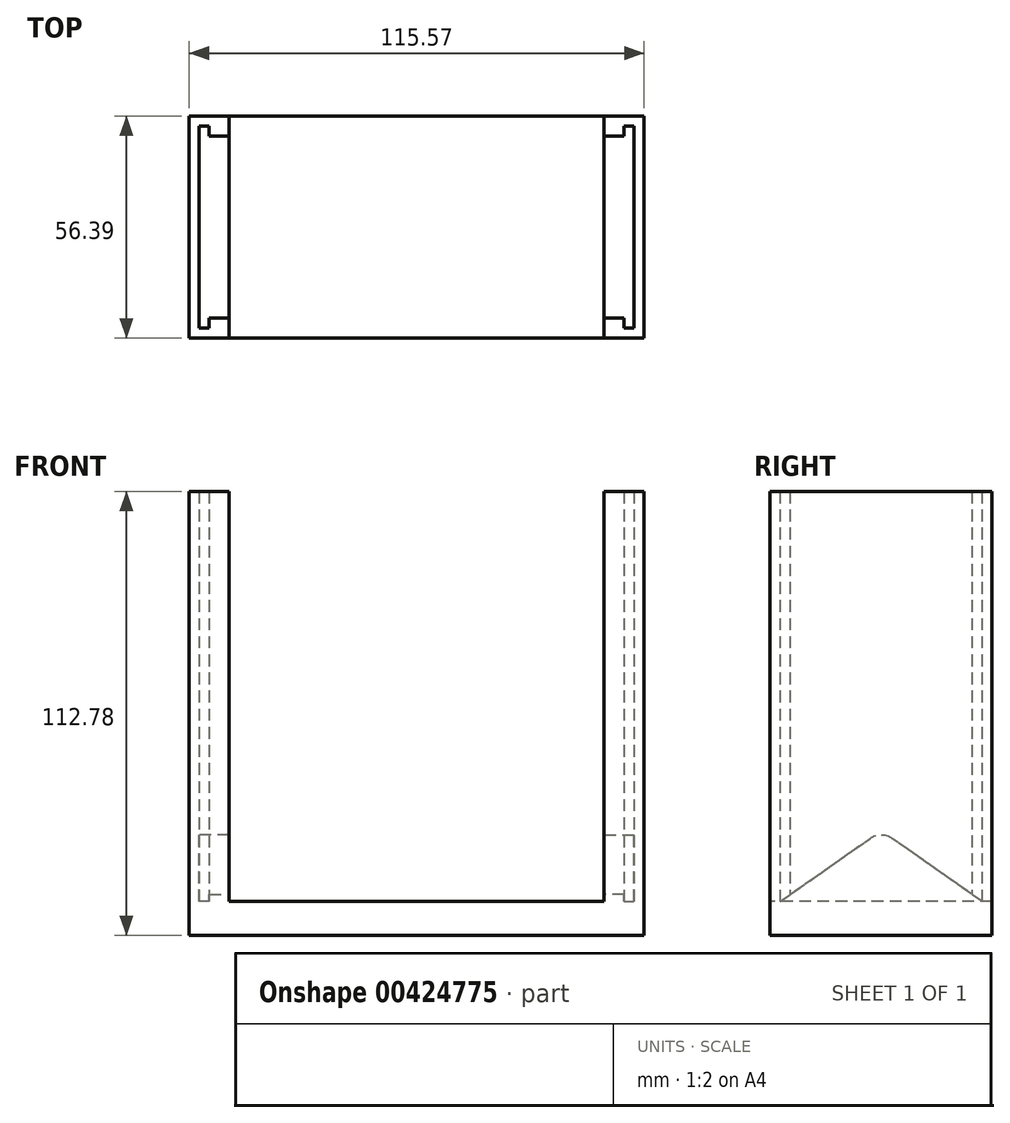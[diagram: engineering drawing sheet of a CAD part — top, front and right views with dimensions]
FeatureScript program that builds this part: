
annotation { "Feature Type Name" : "Feature", "Feature Type Description" : "" }
export const myFeature = defineFeature(function(context is Context, id is Id, definition is map)
    precondition{}
    {
        {
            var Q0;
            Q0=qCreatedBy(makeId("Top.planeOp"),FACE);
            var sketch = newSketch(context, id + "F0", { "sketchPlane" : qUnion([Q0])});
            skLineSegment(sketch, "E0.bottom", {"start": v(-115.57, 0) * mm, "end": v(0, 0) * mm});
            skLineSegment(sketch, "E0.top", {"start": v(-115.57, -56.39) * mm, "end": v(0, -56.39) * mm});
            skLineSegment(sketch, "E0.left", {"start": v(-115.57, 0) * mm, "end": v(-115.57, -56.39) * mm});
            skLineSegment(sketch, "E0.right", {"start": v(0, 0) * mm, "end": v(0, -56.39) * mm});
            skSolve(sketch);
        }
        {
            var Q0;
            Q0=qSketchRegion(id+"F0",true);
            extrude(context, id + "F1", {"entities" : qUnion([Q0]), "depth" : 8.64 * mm});
        }
        {
            var Q0;
            Q0=makeQuery(id+"F1.opExtrude","CAP_FACE",FACE,{"disambiguationData":[OSD([sQuery(id+"F0.wireOp",EDGE,"E0.bottom"),sQuery(id+"F0.wireOp",EDGE,"E0.top"),sQuery(id+"F0.wireOp",EDGE,"E0.left"),sQuery(id+"F0.wireOp",EDGE,"E0.right")])],"isStart":false});
            var sketch = newSketch(context, id + "F2", { "sketchPlane" : qUnion([Q0])});
            skLineSegment(sketch, "E1", {"start": v(0, -28.2) * mm, "end": v(0, -56.39) * mm});
            skLineSegment(sketch, "E2", {"start": v(0, -56.39) * mm, "end": v(-10.16, -56.39) * mm});
            skLineSegment(sketch, "E3", {"start": v(-10.16, -56.39) * mm, "end": v(-10.16, -51.3) * mm});
            skLineSegment(sketch, "E4", {"start": v(-10.16, -51.3) * mm, "end": v(-5.08, -51.3) * mm});
            skLineSegment(sketch, "E5", {"start": v(-5.08, -51.3) * mm, "end": v(-5.08, -53.85) * mm});
            skLineSegment(sketch, "E6", {"start": v(-5.08, -53.85) * mm, "end": v(-2.54, -53.85) * mm});
            skLineSegment(sketch, "E7", {"start": v(-2.54, -53.85) * mm, "end": v(-2.54, -28.2) * mm});
            skLineSegment(sketch, "E8", {"start": v(0, -28.2) * mm, "end": v(-115.57, -28.2) * mm, "construction": true});
            skLineSegment(sketch, "E9", {"start": v(-57.79, 0) * mm, "end": v(-57.79, -56.39) * mm, "construction": true});
            skLineSegment(sketch, "E10.MirrorCS", {"start": v(-2.54, -2.54) * mm, "end": v(-2.54, -28.2) * mm});
            skLineSegment(sketch, "E11.MirrorCS", {"start": v(0, -28.2) * mm, "end": v(0, 0) * mm});
            skLineSegment(sketch, "E12.MirrorCS", {"start": v(-5.08, -2.54) * mm, "end": v(-2.54, -2.54) * mm});
            skLineSegment(sketch, "E13.MirrorCS", {"start": v(0, 0) * mm, "end": v(-10.16, 0) * mm});
            skLineSegment(sketch, "E14.MirrorCS", {"start": v(-10.16, 0) * mm, "end": v(-10.16, -5.08) * mm});
            skLineSegment(sketch, "E15.MirrorCS", {"start": v(-10.16, -5.08) * mm, "end": v(-5.08, -5.08) * mm});
            skLineSegment(sketch, "E16.MirrorCS", {"start": v(-5.08, -5.08) * mm, "end": v(-5.08, -2.54) * mm});
            skLineSegment(sketch, "E17.MirrorCS", {"start": v(-105.4, 0) * mm, "end": v(-105.4, -5.08) * mm});
            skLineSegment(sketch, "E18.MirrorCS", {"start": v(-105.4, -5.08) * mm, "end": v(-110.5, -5.08) * mm});
            skLineSegment(sketch, "E19.MirrorCS", {"start": v(-110.49, -5.08) * mm, "end": v(-110.49, -2.54) * mm});
            skLineSegment(sketch, "E20.MirrorCS", {"start": v(-110.5, -2.54) * mm, "end": v(-113.03, -2.54) * mm});
            skLineSegment(sketch, "E21.MirrorCS", {"start": v(-115.57, 0) * mm, "end": v(-105.41, 0) * mm});
            skLineSegment(sketch, "E22.MirrorCS", {"start": v(-113.03, -2.54) * mm, "end": v(-113.03, -28.2) * mm});
            skLineSegment(sketch, "E23.MirrorCS", {"start": v(-115.57, -28.2) * mm, "end": v(-115.57, 0) * mm});
            skLineSegment(sketch, "E24.MirrorCS", {"start": v(-115.57, -28.2) * mm, "end": v(-115.57, -56.39) * mm});
            skLineSegment(sketch, "E25.MirrorCS", {"start": v(-113.03, -53.85) * mm, "end": v(-113.03, -28.2) * mm});
            skLineSegment(sketch, "E26.MirrorCS", {"start": v(-110.5, -53.85) * mm, "end": v(-113.03, -53.85) * mm});
            skLineSegment(sketch, "E27.MirrorCS", {"start": v(-115.57, -56.39) * mm, "end": v(-105.41, -56.39) * mm});
            skLineSegment(sketch, "E28.MirrorCS", {"start": v(-105.4, -56.39) * mm, "end": v(-105.4, -51.3) * mm});
            skLineSegment(sketch, "E29.MirrorCS", {"start": v(-105.4, -51.3) * mm, "end": v(-110.5, -51.3) * mm});
            skLineSegment(sketch, "E30.MirrorCS", {"start": v(-110.49, -51.3) * mm, "end": v(-110.49, -53.85) * mm});
            skSolve(sketch);
        }
        {
            var Q0;
            Q0=qSketchRegion(id+"F2",true);
            extrude(context, id + "F3", {"entities" : qUnion([Q0]), "operationType" : NewBodyOperationType.ADD, "depth" : 104.14 * mm});
        }
        {
            var Q0;
            Q0=makeQuery(id+"F3.opExtrude","SWEPT_FACE",FACE,{"disambiguationData":[OSD([sQuery(id+"F2.wireOp",EDGE,"E22.MirrorCS"),sQuery(id+"F2.wireOp",EDGE,"E25.MirrorCS")])]});
            var sketch = newSketch(context, id + "F4", { "sketchPlane" : qUnion([Q0])});
            skLineSegment(sketch, "E31", {"start": v(-28.2, 8.64) * mm, "end": v(-28.2, 46.84) * mm, "construction": true});
            skLineSegment(sketch, "E32", {"start": v(-28.2, 8.64) * mm, "end": v(-2.54, 8.64) * mm});
            skLineSegment(sketch, "E33", {"start": v(-2.54, 8.64) * mm, "end": v(-2.54, 8.64) * mm});
            skLineSegment(sketch, "E34", {"start": v(-2.54, 8.64) * mm, "end": v(-25.28, 24.56) * mm});
            skArc(sketch, "E35", {"start": v(-25.28, 24.56) * mm, "mid": v(-26.67, 25.24) * mm, "end": v(-28.2, 25.48) * mm});
            skArc(sketch, "E36.MirrorCS", {"start": v(-31.1, 24.56) * mm, "mid": v(-29.72, 25.24) * mm, "end": v(-28.2, 25.48) * mm});
            skLineSegment(sketch, "E37.MirrorCS", {"start": v(-53.85, 8.64) * mm, "end": v(-31.1, 24.56) * mm});
            skLineSegment(sketch, "E38.MirrorCS", {"start": v(-53.85, 8.64) * mm, "end": v(-53.85, 8.64) * mm});
            skLineSegment(sketch, "E39.MirrorCS", {"start": v(-28.2, 8.64) * mm, "end": v(-53.85, 8.64) * mm});
            skSolve(sketch);
        }
        {
            var Q0;
            Q0=makeQuery(id+"F4.imprint","IMPRINT",FACE,{"disambiguationData":[TD([[makeQuery(id+"F4.imprint","IMPRINT",EDGE,{"derivedFrom":sQuery(id+"F4.wireOp",EDGE,"E32")}),1.0]])]});
            extrude(context, id + "F5", {"entities" : qUnion([Q0]), "operationType" : NewBodyOperationType.ADD, "depth" : 7.62 * mm});
        }
        {
            var Q0;
            Q0=makeQuery(id+"F3.opExtrude","SWEPT_FACE",FACE,{"disambiguationData":[OSD([sQuery(id+"F2.wireOp",EDGE,"E7"),sQuery(id+"F2.wireOp",EDGE,"E10.MirrorCS")])]});
            var sketch = newSketch(context, id + "F6", { "sketchPlane" : qUnion([Q0])});
            skLineSegment(sketch, "E40", {"start": v(28.2, 8.64) * mm, "end": v(28.2, 88.52) * mm, "construction": true});
            skLineSegment(sketch, "E41", {"start": v(28.2, 8.64) * mm, "end": v(53.85, 8.64) * mm});
            skLineSegment(sketch, "E42", {"start": v(53.85, 8.64) * mm, "end": v(53.85, 8.64) * mm});
            skLineSegment(sketch, "E43", {"start": v(53.85, 8.64) * mm, "end": v(31.1, 24.56) * mm});
            skArc(sketch, "E44", {"start": v(31.1, 24.56) * mm, "mid": v(29.72, 25.24) * mm, "end": v(28.2, 25.48) * mm});
            skArc(sketch, "E45.MirrorCS", {"start": v(25.28, 24.56) * mm, "mid": v(26.67, 25.24) * mm, "end": v(28.2, 25.48) * mm});
            skLineSegment(sketch, "E46.MirrorCS", {"start": v(2.54, 8.64) * mm, "end": v(25.28, 24.56) * mm});
            skLineSegment(sketch, "E47.MirrorCS", {"start": v(2.54, 8.64) * mm, "end": v(2.54, 8.64) * mm});
            skLineSegment(sketch, "E48.MirrorCS", {"start": v(28.2, 8.64) * mm, "end": v(2.54, 8.64) * mm});
            skSolve(sketch);
        }
        {
            var Q0;
            Q0=makeQuery(id+"F6.imprint","IMPRINT",FACE,{"disambiguationData":[TD([[makeQuery(id+"F6.imprint","IMPRINT",EDGE,{"derivedFrom":sQuery(id+"F6.wireOp",EDGE,"E41")}),1.0]])]});
            extrude(context, id + "F7", {"entities" : qUnion([Q0]), "operationType" : NewBodyOperationType.ADD, "depth" : 7.62 * mm});
        }
    });
